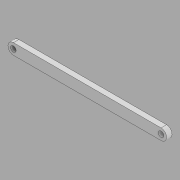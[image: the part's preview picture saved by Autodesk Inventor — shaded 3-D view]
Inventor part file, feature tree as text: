
AUTODESK INVENTOR PART (.ipt)
format: ipt  version: 2020 (Build 240168000, 168)  size: 85,504 bytes
history: native  units: in
note: dims shown in document units (in); Inventor stores cm internally (conversion verified against a paired STEP export)
features: other x1, extrude x1, sketch x1
ambient origin geometry x8: Origin, YZ Plane, XZ Plane, XY Plane, X Axis, Y Axis, Z Axis, Center Point
bodies: Body1 (feature_tree)
feature tree (3):
  other  "Sólido1"
  extrude  "Extrusión1"  Depth=0.125in
  sketch  "Boceto1"  dims[d0=1.6875in d5=0.125in d6=0.125in d7=0.0625in d8=0.0625in d9=0.0625in d10=0.0in]
